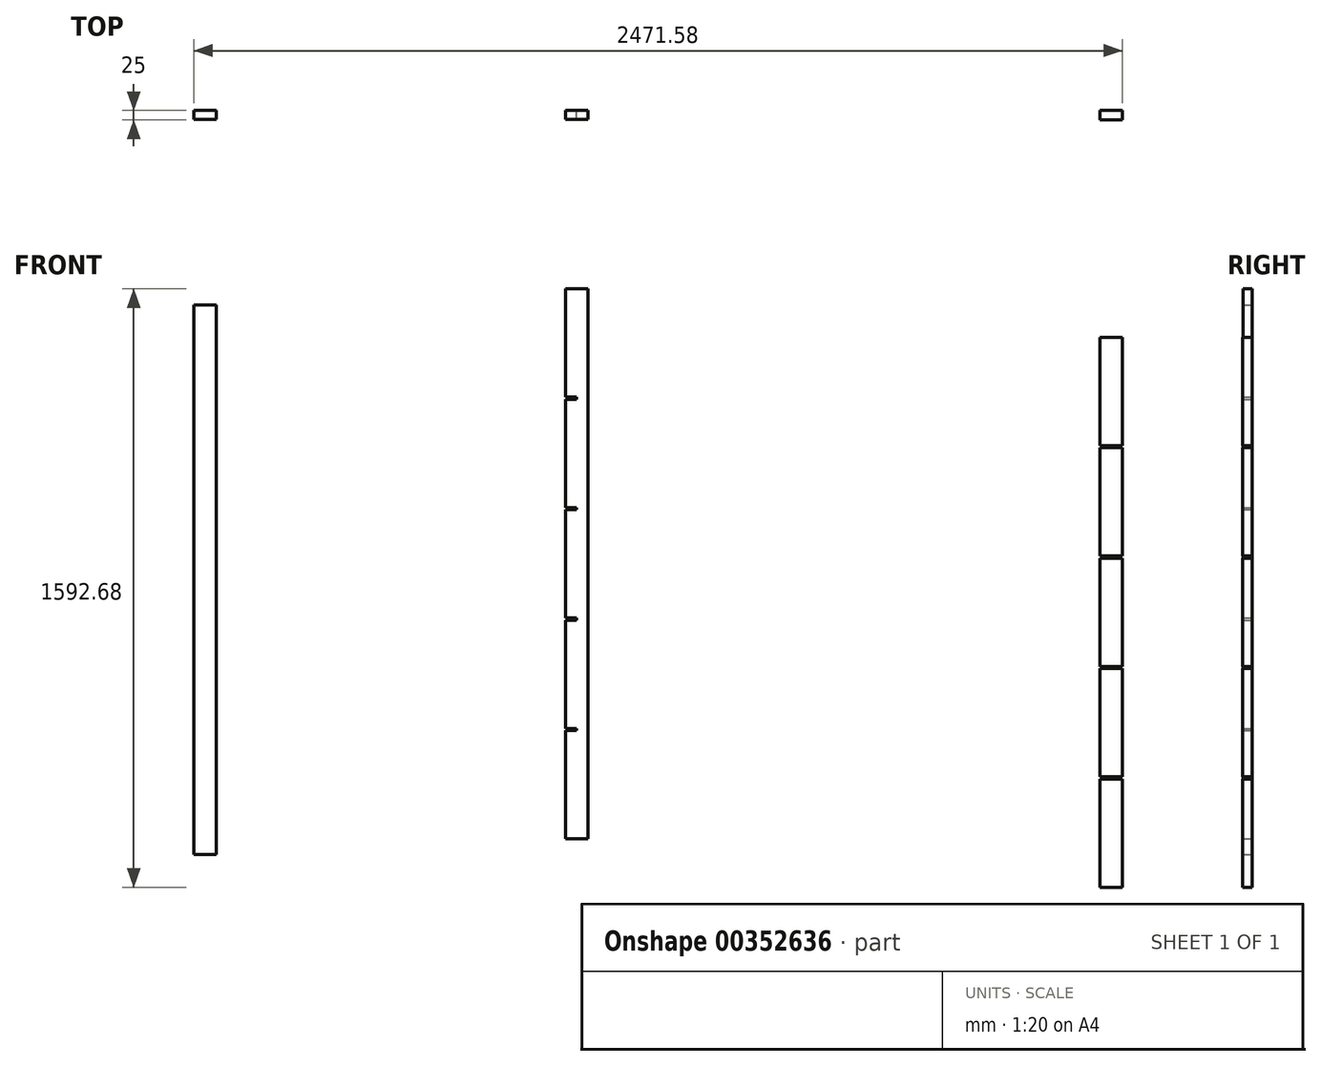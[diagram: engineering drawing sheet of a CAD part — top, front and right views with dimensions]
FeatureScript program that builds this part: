
annotation { "Feature Type Name" : "Feature", "Feature Type Description" : "" }
export const myFeature = defineFeature(function(context is Context, id is Id, definition is map)
    precondition{}
    {
        {
            var Q0;
            Q0=qCreatedBy(makeId("Front.planeOp"),FACE);
            var sketch = newSketch(context, id + "F0", { "sketchPlane" : qUnion([Q0])});
            skLineSegment(sketch, "E0", {"start": v(-361.78, 752.98) * mm, "end": v(-361.78, -711.02) * mm});
            skLineSegment(sketch, "E1", {"start": v(-301.78, 752.98) * mm, "end": v(-301.78, -711.02) * mm});
            skLineSegment(sketch, "E2", {"start": v(-361.78, 752.98) * mm, "end": v(-301.78, 752.98) * mm});
            skLineSegment(sketch, "E3", {"start": v(-361.78, -711.02) * mm, "end": v(-301.78, -711.02) * mm});
            skSolve(sketch);
        }
        {
            var Q0;
            Q0 = qSketchRegion(id + "F0", true);
            extrude(context, id + "F1", {"entities" : qUnion([Q0]), "depth" : 24 * mm, "offsetDistance" : 25 * mm});
        }
        {
            var Q0;
            Q0=qCreatedBy(makeId("Front.planeOp"),FACE);
            var sketch = newSketch(context, id + "F2", { "sketchPlane" : qUnion([Q0])});
            skLineSegment(sketch, "E4", {"start": v(2049.8, 378.25) * mm, "end": v(2109.8, 378.25) * mm});
            skLineSegment(sketch, "E5", {"start": v(2049.8, 84.25) * mm, "end": v(2109.8, 84.25) * mm});
            skLineSegment(sketch, "E6", {"start": v(2049.8, 78.25) * mm, "end": v(2109.8, 78.25) * mm});
            skLineSegment(sketch, "E7", {"start": v(2049.8, -209.75) * mm, "end": v(2109.8, -209.75) * mm});
            skLineSegment(sketch, "E8", {"start": v(2049.8, -215.75) * mm, "end": v(2109.8, -215.75) * mm});
            skLineSegment(sketch, "E9", {"start": v(2049.8, -503.75) * mm, "end": v(2109.8, -503.75) * mm});
            skLineSegment(sketch, "E10", {"start": v(2049.8, -509.75) * mm, "end": v(2109.8, -509.75) * mm});
            skLineSegment(sketch, "E11", {"start": v(2049.8, 666.25) * mm, "end": v(2109.8, 666.25) * mm});
            skLineSegment(sketch, "E12", {"start": v(2049.8, -797.75) * mm, "end": v(2109.8, -797.75) * mm});
            skLineSegment(sketch, "E13", {"start": v(2049.8, 372.25) * mm, "end": v(2109.8, 372.25) * mm});
            skLineSegment(sketch, "E14", {"start": v(2049.8, 666.25) * mm, "end": v(2049.8, -797.75) * mm});
            skLineSegment(sketch, "E15", {"start": v(2109.8, -797.75) * mm, "end": v(2109.8, 666.25) * mm});
            skSolve(sketch);
        }
        {
            var Q0;
            {var subQ0=sQuery(id+"F2.wireOp",EDGE,"E4");Q0=makeQuery(id+"F2.imprint","IMPRINT",FACE,{"disambiguationData":[TD([[makeQuery(id+"F2.imprint","IMPRINT",EDGE,{"derivedFrom":subQ0}),1.0]])]});}
            var Q1;
            {var subQ0=sQuery(id+"F2.wireOp",EDGE,"E5");Q1=makeQuery(id+"F2.imprint","IMPRINT",FACE,{"disambiguationData":[TD([[makeQuery(id+"F2.imprint","IMPRINT",EDGE,{"derivedFrom":subQ0}),1.0]])]});}
            var Q2;
            {var subQ0=sQuery(id+"F2.wireOp",EDGE,"E6");Q2=makeQuery(id+"F2.imprint","IMPRINT",FACE,{"disambiguationData":[TD([[makeQuery(id+"F2.imprint","IMPRINT",EDGE,{"derivedFrom":subQ0}),-1.0]])]});}
            var Q3;
            {var subQ0=sQuery(id+"F2.wireOp",EDGE,"E8");Q3=makeQuery(id+"F2.imprint","IMPRINT",FACE,{"disambiguationData":[TD([[makeQuery(id+"F2.imprint","IMPRINT",EDGE,{"derivedFrom":subQ0}),-1.0]])]});}
            var Q4;
            {var subQ0=sQuery(id+"F2.wireOp",EDGE,"E10");Q4=makeQuery(id+"F2.imprint","IMPRINT",FACE,{"disambiguationData":[TD([[makeQuery(id+"F2.imprint","IMPRINT",EDGE,{"derivedFrom":subQ0}),-1.0]])]});}
            extrude(context, id + "F3", {"entities" : qUnion([Q0, Q1, Q2, Q3, Q4]), "depth" : 25 * mm, "offsetDistance" : 25 * mm});
        }
        {
            var Q0;
            Q0=qCreatedBy(makeId("Front.planeOp"),FACE);
            var sketch = newSketch(context, id + "F4", { "sketchPlane" : qUnion([Q0])});
            skLineSegment(sketch, "E16", {"start": v(627.51, 506.93) * mm, "end": v(657.51, 506.93) * mm});
            skLineSegment(sketch, "E17", {"start": v(627.51, 212.93) * mm, "end": v(657.51, 212.93) * mm});
            skLineSegment(sketch, "E18", {"start": v(627.51, 206.93) * mm, "end": v(657.51, 206.93) * mm});
            skLineSegment(sketch, "E19", {"start": v(627.51, -81.07) * mm, "end": v(657.51, -81.07) * mm});
            skLineSegment(sketch, "E20", {"start": v(627.51, -87.07) * mm, "end": v(657.51, -87.07) * mm});
            skLineSegment(sketch, "E21", {"start": v(627.51, -375.07) * mm, "end": v(657.51, -375.07) * mm});
            skLineSegment(sketch, "E22", {"start": v(627.51, -381.07) * mm, "end": v(657.51, -381.07) * mm});
            skLineSegment(sketch, "E23", {"start": v(627.51, 794.93) * mm, "end": v(687.51, 794.93) * mm});
            skLineSegment(sketch, "E24", {"start": v(627.51, -669.07) * mm, "end": v(687.51, -669.07) * mm});
            skLineSegment(sketch, "E25", {"start": v(627.51, 500.93) * mm, "end": v(657.51, 500.93) * mm});
            skLineSegment(sketch, "E26", {"start": v(627.51, 794.93) * mm, "end": v(627.51, 506.93) * mm});
            skLineSegment(sketch, "E27", {"start": v(687.51, -669.07) * mm, "end": v(687.51, 794.93) * mm});
            skLineSegment(sketch, "E28", {"start": v(657.51, 506.93) * mm, "end": v(657.51, 500.93) * mm});
            skPoint(sketch, "E29.orphan", {"position": v(657.51, 794.93) * mm});
            skLineSegment(sketch, "E30.trimOffspring", {"start": v(657.51, 212.93) * mm, "end": v(657.51, 206.93) * mm});
            skLineSegment(sketch, "E31.trimOffspring", {"start": v(657.51, -81.07) * mm, "end": v(657.51, -87.07) * mm});
            skLineSegment(sketch, "E32.trimOffspring", {"start": v(657.51, -375.07) * mm, "end": v(657.51, -381.07) * mm});
            skPoint(sketch, "E33.orphan", {"position": v(657.51, -669.07) * mm});
            skLineSegment(sketch, "E34.trimOffspring", {"start": v(627.51, 500.93) * mm, "end": v(627.51, 212.93) * mm});
            skLineSegment(sketch, "E35.trimOffspring", {"start": v(627.51, 206.93) * mm, "end": v(627.51, -81.07) * mm});
            skLineSegment(sketch, "E36.trimOffspring", {"start": v(627.51, -87.07) * mm, "end": v(627.51, -375.07) * mm});
            skLineSegment(sketch, "E37.trimOffspring", {"start": v(627.51, -381.07) * mm, "end": v(627.51, -669.07) * mm});
            skSolve(sketch);
        }
        {
            var Q0;
            Q0 = qSketchRegion(id + "F4", true);
            extrude(context, id + "F5", {"entities" : qUnion([Q0]), "depth" : 24 * mm, "offsetDistance" : 25 * mm});
        }
    });
